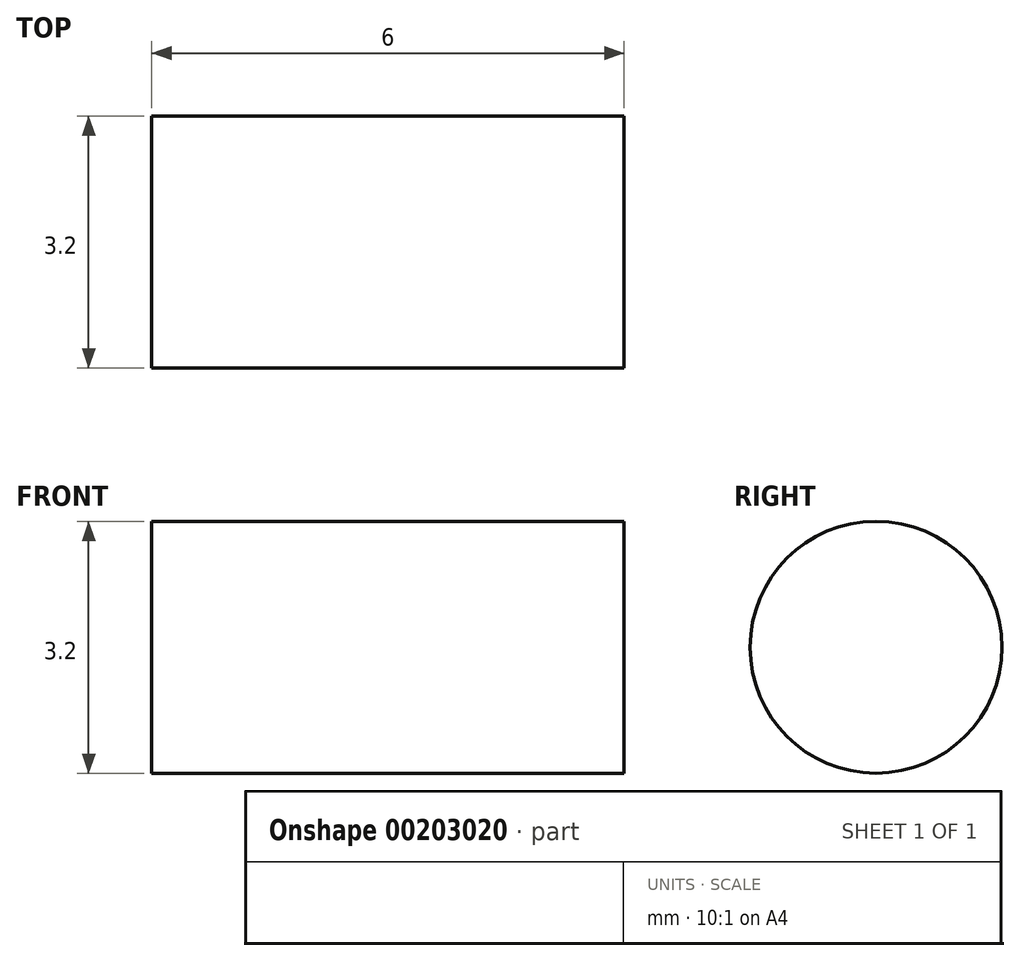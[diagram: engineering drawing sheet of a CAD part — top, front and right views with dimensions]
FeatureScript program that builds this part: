
annotation { "Feature Type Name" : "Feature", "Feature Type Description" : "" }
export const myFeature = defineFeature(function(context is Context, id is Id, definition is map)
    precondition{}
    {
        {
            var Q0;
            Q0=qCreatedBy(makeId("Right.planeOp"),FACE);
            var sketch = newSketch(context, id + "F0", { "sketchPlane" : qUnion([Q0])});
            skCircle(sketch, "E0", {"center": v(11.6, -84.57) * mm, "radius": 1.6 * mm});
            skCircle(sketch, "E1", {"center": v(42.6, -84.57) * mm, "radius": 1.6 * mm});
            skCircle(sketch, "E2", {"center": v(42.6, -53.57) * mm, "radius": 1.6 * mm});
            skCircle(sketch, "E3", {"center": v(11.6, -53.57) * mm, "radius": 1.6 * mm});
            skLineSegment(sketch, "E4", {"start": v(5.6, -85.57) * mm, "end": v(5.6, -47.58) * mm});
            skArc(sketch, "E5", {"start": v(5.6, -47.58) * mm, "mid": v(5.6, -47.57) * mm, "end": v(5.6, -47.56) * mm});
            skLineSegment(sketch, "E6", {"start": v(5.6, -47.56) * mm, "end": v(5.52, -21.58) * mm});
            skArc(sketch, "E7", {"start": v(5.52, -21.58) * mm, "mid": v(6.97, -18.04) * mm, "end": v(10.52, -16.57) * mm});
            skLineSegment(sketch, "E8", {"start": v(10.52, -16.57) * mm, "end": v(43.68, -16.57) * mm});
            skArc(sketch, "E9", {"start": v(43.68, -16.57) * mm, "mid": v(47.23, -18.04) * mm, "end": v(48.68, -21.58) * mm});
            skLineSegment(sketch, "E10", {"start": v(48.68, -21.58) * mm, "end": v(48.6, -47.56) * mm});
            skArc(sketch, "E11", {"start": v(48.6, -47.56) * mm, "mid": v(48.6, -47.57) * mm, "end": v(48.6, -47.58) * mm});
            skLineSegment(sketch, "E12", {"start": v(48.6, -47.58) * mm, "end": v(48.6, -85.57) * mm});
            skArc(sketch, "E13", {"start": v(48.6, -85.57) * mm, "mid": v(47.14, -89.1) * mm, "end": v(43.6, -90.57) * mm});
            skLineSegment(sketch, "E14", {"start": v(43.6, -90.57) * mm, "end": v(10.6, -90.57) * mm});
            skArc(sketch, "E15", {"start": v(10.6, -90.57) * mm, "mid": v(7.06, -89.1) * mm, "end": v(5.6, -85.57) * mm});
            skCircle(sketch, "E16", {"center": v(37.1, -36.57) * mm, "radius": 1.6 * mm});
            skCircle(sketch, "E17", {"center": v(17.1, -36.57) * mm, "radius": 1.6 * mm});
            skCircle(sketch, "E18", {"center": v(17.1, -26.57) * mm, "radius": 1.6 * mm});
            skCircle(sketch, "E19", {"center": v(37.1, -26.57) * mm, "radius": 1.6 * mm});
            skCircle(sketch, "E20", {"center": v(27.1, -69.07) * mm, "radius": 3 * mm});
            skSolve(sketch);
        }
        {
            var Q0;
            Q0=makeQuery(id+"F0.imprint","IMPRINT",FACE,{"disambiguationData":[TD([[makeQuery(id+"F0.imprint","IMPRINT",EDGE,{"derivedFrom":sQuery(id+"F0.wireOp",EDGE,"E0")}),1.0]])]});
            extrude(context, id + "F1", {"entities" : qUnion([Q0]), "depth" : 6 * mm});
        }
    });
